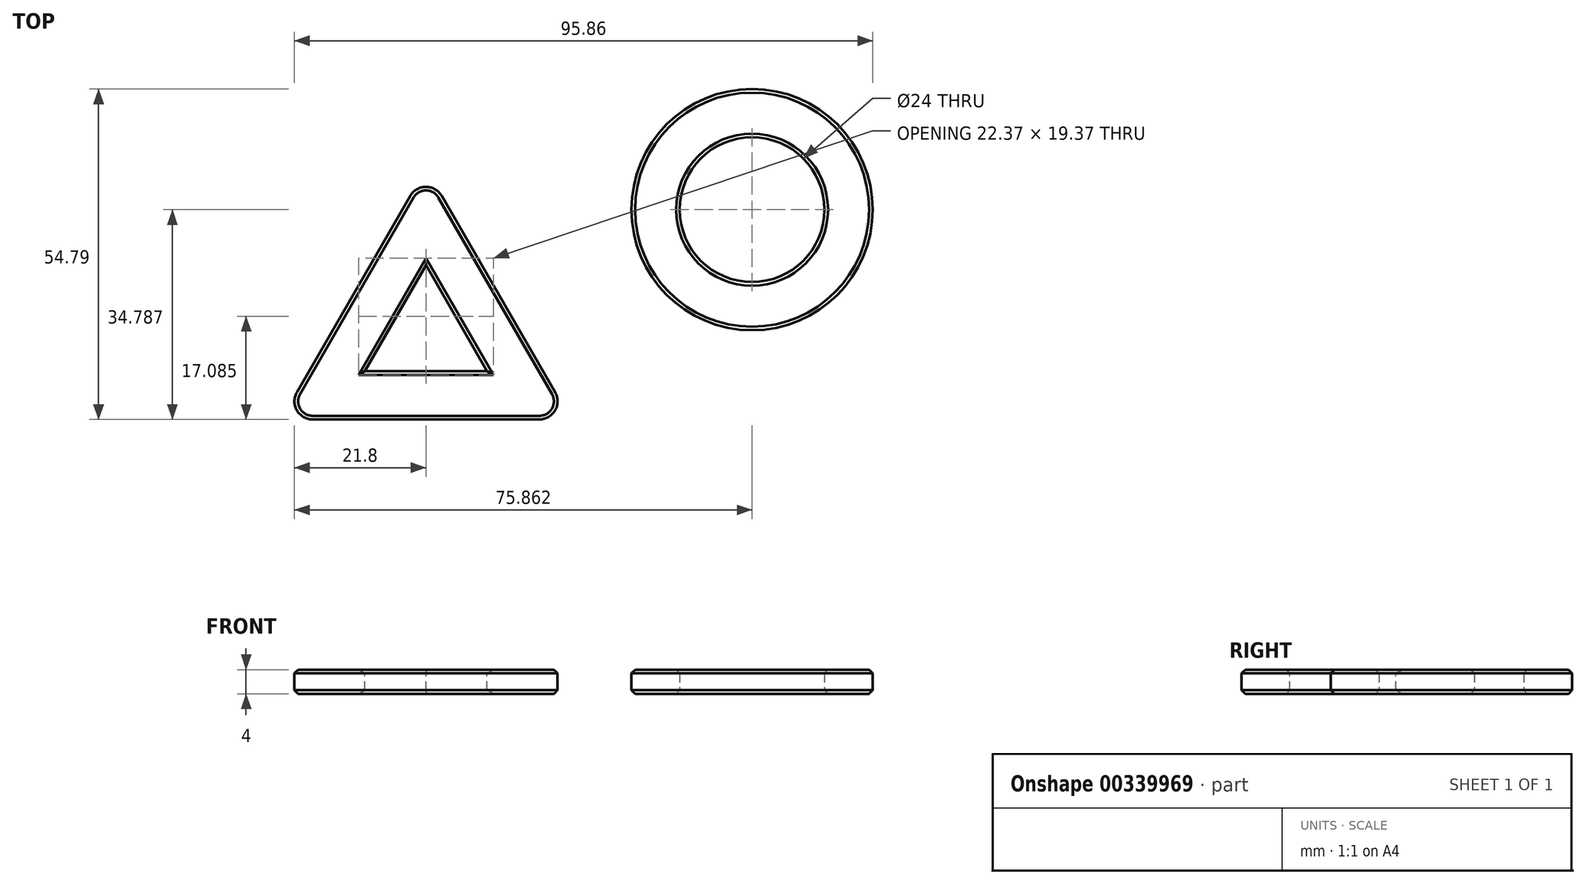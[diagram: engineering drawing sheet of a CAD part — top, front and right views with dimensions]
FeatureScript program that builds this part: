
annotation { "Feature Type Name" : "Feature", "Feature Type Description" : "" }
export const myFeature = defineFeature(function(context is Context, id is Id, definition is map)
    precondition{}
    {
        {
            var Q0;
            Q0=qCreatedBy(makeId("Top.planeOp"),FACE);
            var sketch = newSketch(context, id + "F0", { "sketchPlane" : qUnion([Q0])});
            skLineSegment(sketch, "E0", {"start": v(0, 0) * mm, "end": v(24, 0) * mm});
            skLineSegment(sketch, "E1", {"start": v(24, 0) * mm, "end": v(0, 41.57) * mm});
            skLineSegment(sketch, "E2", {"start": v(0, 41.57) * mm, "end": v(-24, 0) * mm});
            skLineSegment(sketch, "E3", {"start": v(-24, 0) * mm, "end": v(0, 0) * mm});
            skSolve(sketch);
        }
        {
            var Q0;
            Q0 = qSketchRegion(id + "F0", true);
            extrude(context, id + "F1", {"entities" : qUnion([Q0]), "depth" : 4 * mm, "offsetDistance" : 25 * mm});
        }
        {
            var Q0;
            Q0=makeQuery(id+"F1.opExtrude","CAP_FACE",FACE,{"disambiguationData":[OSD([sQuery(id+"F0.wireOp",EDGE,"E0"),sQuery(id+"F0.wireOp",EDGE,"E1"),sQuery(id+"F0.wireOp",EDGE,"E2"),sQuery(id+"F0.wireOp",EDGE,"E3")])],"isStart":false});
            var sketch = newSketch(context, id + "F2", { "sketchPlane" : qUnion([Q0])});
            skLineSegment(sketch, "E4.0", {"start": v(-10.14, 8) * mm, "end": v(10.14, 8) * mm});
            skLineSegment(sketch, "E4.1", {"start": v(0, 25.57) * mm, "end": v(-10.14, 8) * mm});
            skLineSegment(sketch, "E4.2", {"start": v(10.14, 8) * mm, "end": v(0, 25.57) * mm});
            skSolve(sketch);
        }
        {
            var Q0;
            Q0=makeQuery(id+"F2.imprint","IMPRINT",FACE,{"disambiguationData":[TD([[makeQuery(id+"F2.imprint","IMPRINT",EDGE,{"derivedFrom":sQuery(id+"F2.wireOp",EDGE,"E4.0")}),1.0]])]});
            extrude(context, id + "F3", {"entities" : qUnion([Q0]), "operationType" : NewBodyOperationType.REMOVE, "oppositeDirection" : true, "depth" : 25 * mm, "offsetDistance" : 25 * mm});
        }
        {
            var Q0;
            Q0=makeQuery(id+"F1.opExtrude","SWEPT_EDGE",EDGE,{"disambiguationData":[OSD([sQuery(id+"F0.wireOp",EDGE,"E2"),sQuery(id+"F0.wireOp",EDGE,"E3")])]});
            var Q1;
            Q1=makeQuery(id+"F1.opExtrude","SWEPT_EDGE",EDGE,{"disambiguationData":[OSD([sQuery(id+"F0.wireOp",EDGE,"E0"),sQuery(id+"F0.wireOp",EDGE,"E1")])]});
            var Q2;
            Q2=makeQuery(id+"F1.opExtrude","SWEPT_EDGE",EDGE,{"disambiguationData":[OSD([sQuery(id+"F0.wireOp",EDGE,"E1"),sQuery(id+"F0.wireOp",EDGE,"E2")])]});
            fillet(context, id + "F4", {"entities" : qUnion([Q0, Q1, Q2]), "radius" : 3 * mm, "tangentPropagation" : true, "allowEdgeOverflow" : false});
        }
        {
            var Q0;
            Q0=makeQuery(id+"F1.opExtrude","CAP_FACE",FACE,{"disambiguationData":[OSD([sQuery(id+"F0.wireOp",EDGE,"E0"),sQuery(id+"F0.wireOp",EDGE,"E1"),sQuery(id+"F0.wireOp",EDGE,"E2"),sQuery(id+"F0.wireOp",EDGE,"E3")])],"isStart":false});
            var Q1;
            Q1=makeQuery(id+"F1.opExtrude","CAP_FACE",FACE,{"disambiguationData":[OSD([sQuery(id+"F0.wireOp",EDGE,"E0"),sQuery(id+"F0.wireOp",EDGE,"E1"),sQuery(id+"F0.wireOp",EDGE,"E2"),sQuery(id+"F0.wireOp",EDGE,"E3")])],"isStart":true});
            chamfer(context, id + "F5", {"entities" : qUnion([Q0, Q1]), "width" : 0.6 * mm, "tangentPropagation" : true});
        }
        {
            var Q0;
            Q0=qCreatedBy(makeId("Top.planeOp"),FACE);
            var sketch = newSketch(context, id + "F6", { "sketchPlane" : qUnion([Q0])});
            skCircle(sketch, "E5", {"center": v(54.06, 34.79) * mm, "radius": 20 * mm});
            skCircle(sketch, "E6", {"center": v(54.06, 34.79) * mm, "radius": 12 * mm});
            skSolve(sketch);
        }
        {
            var Q0;
            Q0 = qSketchRegion(id + "F6", true);
            extrude(context, id + "F7", {"entities" : qUnion([Q0]), "depth" : 4 * mm, "offsetDistance" : 25 * mm});
        }
        {
            var Q0;
            Q0=makeQuery(id+"F7.opExtrude","CAP_FACE",FACE,{"disambiguationData":[OSD([sQuery(id+"F6.wireOp",EDGE,"E5"),sQuery(id+"F6.wireOp",EDGE,"E6")])],"isStart":false});
            var Q1;
            Q1=makeQuery(id+"F7.opExtrude","CAP_FACE",FACE,{"disambiguationData":[OSD([sQuery(id+"F6.wireOp",EDGE,"E5"),sQuery(id+"F6.wireOp",EDGE,"E6")])],"isStart":true});
            chamfer(context, id + "F8", {"entities" : qUnion([Q0, Q1]), "width" : 0.6 * mm, "tangentPropagation" : true});
        }
    });
